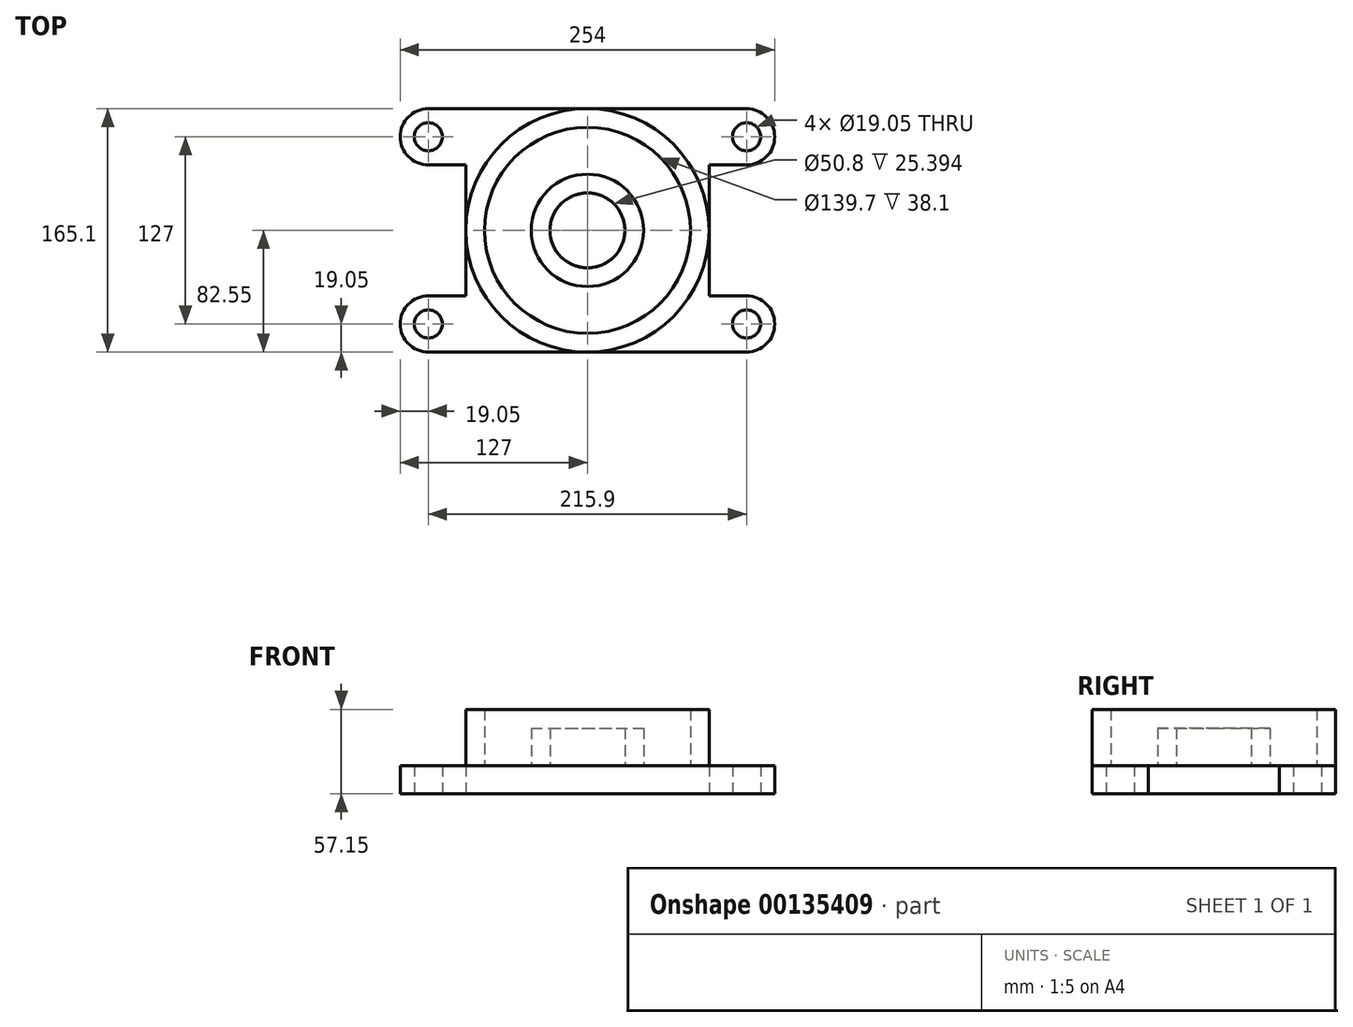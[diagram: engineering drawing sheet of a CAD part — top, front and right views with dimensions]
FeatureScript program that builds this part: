
annotation { "Feature Type Name" : "Feature", "Feature Type Description" : "" }
export const myFeature = defineFeature(function(context is Context, id is Id, definition is map)
    precondition{}
    {
        {
            var Q0;
            Q0=qCreatedBy(makeId("Front.planeOp"),FACE);
            var sketch = newSketch(context, id + "F0", { "sketchPlane" : qUnion([Q0])});
            skLineSegment(sketch, "E0", {"start": v(-82.55, 0) * mm, "end": v(-82.55, 57.15) * mm});
            skLineSegment(sketch, "E1", {"start": v(-25.4, 19.06) * mm, "end": v(-25.4, 44.45) * mm});
            skLineSegment(sketch, "E2", {"start": v(-25.4, 44.45) * mm, "end": v(-38.1, 44.45) * mm});
            skLineSegment(sketch, "E3", {"start": v(-38.1, 44.45) * mm, "end": v(-38.1, 12.7) * mm});
            skLineSegment(sketch, "E4", {"start": v(-38.1, 12.7) * mm, "end": v(-69.85, 12.7) * mm});
            skLineSegment(sketch, "E5", {"start": v(-82.55, 57.15) * mm, "end": v(-69.85, 57.15) * mm});
            skLineSegment(sketch, "E6", {"start": v(-69.85, 57.15) * mm, "end": v(-69.85, 12.7) * mm});
            skLineSegment(sketch, "E7", {"start": v(-6.35, 0) * mm, "end": v(-82.55, 0) * mm});
            skLineSegment(sketch, "E8", {"start": v(-25.4, 19.06) * mm, "end": v(-6.35, 19.06) * mm});
            skLineSegment(sketch, "E9", {"start": v(-6.35, 19.06) * mm, "end": v(-6.35, 0) * mm});
            skLineSegment(sketch, "E10", {"start": v(0, -2.28) * mm, "end": v(0, 18.58) * mm});
            skSolve(sketch);
        }
        {
            var Q0;
            Q0=makeQuery(id+"F0.imprint","IMPRINT",FACE,{"disambiguationData":[TD([[makeQuery(id+"F0.imprint","IMPRINT",EDGE,{"derivedFrom":sQuery(id+"F0.wireOp",EDGE,"E0")}),-1.0]])]});
            var Q1;
            Q1=sQuery(id+"F0.wireOp",EDGE,"E10");
            revolve(context, id + "F1", {"entities" : qUnion([Q0]), "axis" : qUnion([Q1]), "revolveType" : RevolveType.FULL});
        }
        {
            var Q0;
            Q0=qCreatedBy(makeId("Top.planeOp"),FACE);
            var sketch = newSketch(context, id + "F2", { "sketchPlane" : qUnion([Q0])});
            skLineSegment(sketch, "E11", {"start": v(0, 82.55) * mm, "end": v(107.95, 82.55) * mm});
            skArc(sketch, "E12", {"start": v(107.95, 44.45) * mm, "mid": v(127, 63.5) * mm, "end": v(107.95, 82.55) * mm});
            skLineSegment(sketch, "E13", {"start": v(107.95, 44.45) * mm, "end": v(82.55, 44.45) * mm});
            skLineSegment(sketch, "E14", {"start": v(82.55, 44.45) * mm, "end": v(82.55, 0) * mm});
            skCircle(sketch, "E15", {"center": v(107.95, 63.5) * mm, "radius": 9.53 * mm});
            skLineSegment(sketch, "E16", {"start": v(107.95, 82.55) * mm, "end": v(107.95, 73.03) * mm});
            skLineSegment(sketch, "E17.trimOffspring", {"start": v(107.95, 53.98) * mm, "end": v(107.95, 44.45) * mm});
            skLineSegment(sketch, "E18.MirrorCS", {"start": v(0, 82.55) * mm, "end": v(-107.95, 82.55) * mm});
            skArc(sketch, "E19.MirrorCS", {"start": v(-107.95, 44.45) * mm, "mid": v(-127, 63.5) * mm, "end": v(-107.95, 82.55) * mm});
            skCircle(sketch, "E20.MirrorC", {"center": v(-107.95, 63.5) * mm, "radius": 9.53 * mm});
            skLineSegment(sketch, "E21.MirrorCS", {"start": v(-107.95, 44.45) * mm, "end": v(-82.55, 44.45) * mm});
            skLineSegment(sketch, "E22.MirrorCS", {"start": v(-82.55, 44.45) * mm, "end": v(-82.55, 0) * mm});
            skArc(sketch, "E23.MirrorCS", {"start": v(-107.95, -44.45) * mm, "mid": v(-127, -63.5) * mm, "end": v(-107.95, -82.55) * mm});
            skLineSegment(sketch, "E24.MirrorCS", {"start": v(-107.95, -44.45) * mm, "end": v(-82.55, -44.45) * mm});
            skCircle(sketch, "E25.MirrorC", {"center": v(-107.95, -63.5) * mm, "radius": 9.53 * mm});
            skLineSegment(sketch, "E26.MirrorCS", {"start": v(0, -82.55) * mm, "end": v(-107.95, -82.55) * mm});
            skLineSegment(sketch, "E27.MirrorCS", {"start": v(-82.55, -44.45) * mm, "end": v(-82.55, 0) * mm});
            skLineSegment(sketch, "E28.MirrorCS", {"start": v(107.95, -44.45) * mm, "end": v(82.55, -44.45) * mm});
            skArc(sketch, "E29.MirrorCS", {"start": v(107.95, -44.45) * mm, "mid": v(127, -63.5) * mm, "end": v(107.95, -82.55) * mm});
            skCircle(sketch, "E30.MirrorC", {"center": v(107.95, -63.5) * mm, "radius": 9.53 * mm});
            skLineSegment(sketch, "E31.MirrorCS", {"start": v(107.95, -82.55) * mm, "end": v(107.95, -73.03) * mm});
            skLineSegment(sketch, "E32.MirrorCS", {"start": v(82.55, -44.45) * mm, "end": v(82.55, 0) * mm});
            skLineSegment(sketch, "E33.MirrorCS", {"start": v(0, -82.55) * mm, "end": v(107.95, -82.55) * mm});
            skSolve(sketch);
        }
        {
            var Q0;
            Q0=makeQuery(id+"F2.imprint","IMPRINT",FACE,{"disambiguationData":[TD([[makeQuery(id+"F2.imprint","IMPRINT",EDGE,{"derivedFrom":sQuery(id+"F2.wireOp",EDGE,"E11")}),-1.0]])]});
            var Q1;
            Q1=makeQuery(id+"F2.imprint","IMPRINT",FACE,{"disambiguationData":[TD([[makeQuery(id+"F2.imprint","IMPRINT",EDGE,{"derivedFrom":sQuery(id+"F2.wireOp",EDGE,"E12")}),1.0]])]});
            extrude(context, id + "F3", {"entities" : qUnion([Q0, Q1]), "operationType" : NewBodyOperationType.ADD, "depth" : 19.05 * mm});
        }
    });
